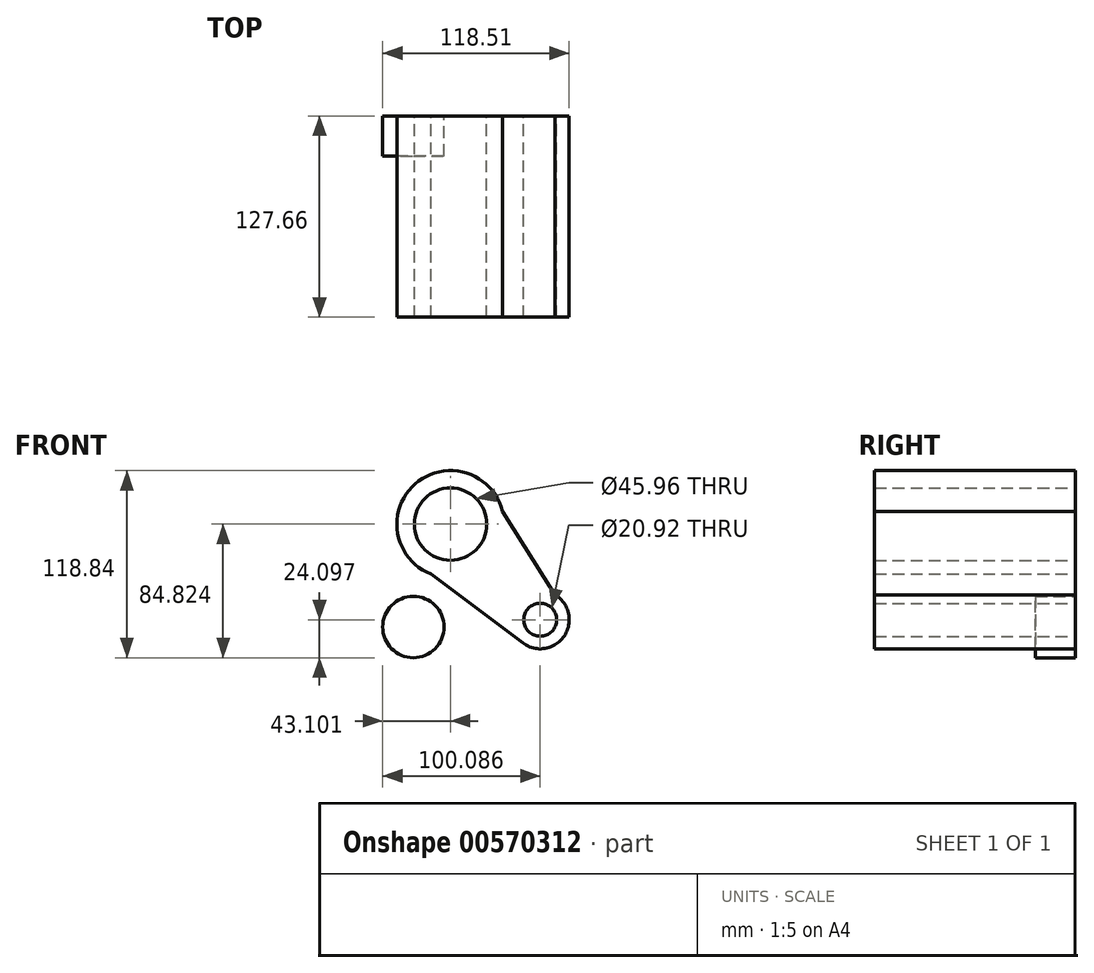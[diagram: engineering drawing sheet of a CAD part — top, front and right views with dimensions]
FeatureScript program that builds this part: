
annotation { "Feature Type Name" : "Feature", "Feature Type Description" : "" }
export const myFeature = defineFeature(function(context is Context, id is Id, definition is map)
    precondition{}
    {
        {
            var Q0;
            Q0=qCreatedBy(makeId("Front.planeOp"),FACE);
            var sketch = newSketch(context, id + "F0", { "sketchPlane" : qUnion([Q0])});
            skCircle(sketch, "E0", {"center": v(-39.43, 38.85) * mm, "radius": 34.01 * mm});
            skCircle(sketch, "E1", {"center": v(17.56, -21.87) * mm, "radius": 18.43 * mm});
            skLineSegment(sketch, "E2", {"start": v(-51.86, 7.2) * mm, "end": v(6.5, -36.61) * mm});
            skLineSegment(sketch, "E3", {"start": v(-6.42, 47.05) * mm, "end": v(27.03, -6.07) * mm});
            skCircle(sketch, "E4", {"center": v(-39.43, 38.85) * mm, "radius": 22.98 * mm});
            skCircle(sketch, "E5", {"center": v(17.56, -21.87) * mm, "radius": 10.46 * mm});
            skSolve(sketch);
        }
        {
            var Q0;
            Q0 = qSketchRegion(id + "F0", true);
            extrude(context, id + "F1", {"entities" : qUnion([Q0]), "depth" : 127.66 * mm, "offsetDistance" : 25.4 * mm});
        }
        {
            var Q0;
            Q0=qCreatedBy(makeId("Front.planeOp"),FACE);
            var sketch = newSketch(context, id + "F2", { "sketchPlane" : qUnion([Q0])});
            skCircle(sketch, "E6", {"center": v(-63.03, -26.48) * mm, "radius": 19.5 * mm});
            skLineSegment(sketch, "E7", {"start": v(-73.97, 38.57) * mm, "end": v(-79.8, -16.54) * mm});
            skLineSegment(sketch, "E8", {"start": v(11.8, -40.87) * mm, "end": v(-49.88, -40.87) * mm});
            skSolve(sketch);
        }
        {
            var Q0;
            Q0 = qSketchRegion(id + "F2", true);
            extrude(context, id + "F3", {"entities" : qUnion([Q0]), "depth" : 25.4 * mm, "offsetDistance" : 25.4 * mm});
        }
    });
